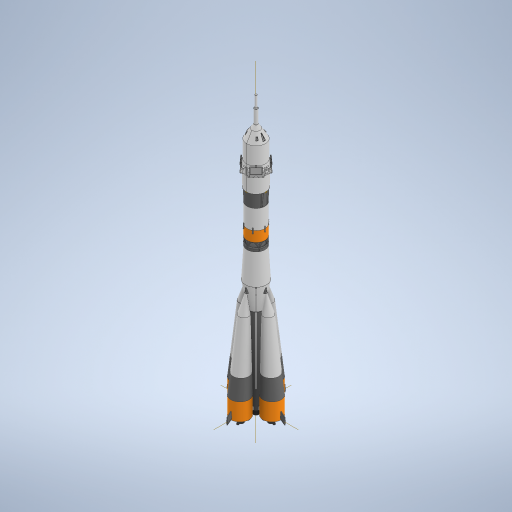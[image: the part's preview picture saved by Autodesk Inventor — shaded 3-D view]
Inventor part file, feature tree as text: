
AUTODESK INVENTOR PART (.ipt)
format: ipt  version: 2023 (Build 270158030, 158C)  size: 15,453,696 bytes
history: native  units: mm
features: fillet x71, sketch x70, extrude x63, other x23, plane x15, revolve x12, pattern_circular x11, sweep x6, mirror x3, chamfer x1, split x1
ambient origin geometry x8: Origin, YZ Plane, XZ Plane, XY Plane, X Axis, Y Axis, Z Axis, Center Point
bodies: Solid17 (feature_tree), Solid18 (feature_tree), Solid19 (feature_tree), Solid20 (feature_tree)
feature tree (276):
  other  "Soyuz Core Stage"
  extrude  "Core Airframe"  Depth=133.0mm TaperAngle=0.0deg
  extrude  "Vernier Housing"  Depth=3.4mm
  extrude  "Main Engine Extrude"  TaperAngle=0.0deg  [1 undecoded]
  extrude  "Main Engine Cut"  Depth=3.4mm
  extrude  "Vernier Nozzels"  Depth=3.4mm
  extrude  "Extrusion11"  Depth=3.4mm
  extrude  "Extrusion12"  Depth=5.5mm
  sweep  "Sweep1"
  sweep  "Booster Nosecone"
  extrude  "Extrusion16"  Depth=4.5mm
  plane  "Work Plane6"
  extrude  "Extrusion17"  Depth=4.5mm
  plane  "Work Plane5"
  extrude  "Extrusion18"  Depth=4.5mm
  fillet  "Fillet11"  Radius=4.5mm
  fillet  "Fillet12"  Radius=6.0mm
  fillet  "Fillet13"  Radius=2.0mm
  fillet  "Fillet14"  Radius=10.5mm
  extrude  "Booster Lock Extrusion"  Depth=2.0mm
  extrude  "Booster Lock Cut"  Depth=10.5mm
  other  "Work Point1"
  plane  "Work Plane1"
  sweep  "Sweep4"
  extrude  "Extrusion26"  TaperAngle=0.0deg  [1 undecoded]
  fillet  "Fillet16"  [1 undecoded]
  plane  "Work Plane4"
  other  "Work Point2"
  plane  "Work Plane2"
  extrude  "Extrusion27"  Depth=5.0mm
  extrude  "Extrusion28"  Depth=5.0mm
  extrude  "Extrusion29"  Depth=5.0mm
  fillet  "Fillet17"  [1 undecoded]
  fillet  "Fillet18"  [1 undecoded]
  fillet  "Fillet19"  [1 undecoded]
  extrude  "Extrusion30"  Depth=9.0mm
  fillet  "Fillet20"  Radius=28.0mm
  fillet  "Fillet21"  Radius=25.0mm
  fillet  "Fillet22"  [1 undecoded]
  extrude  "Extrusion31"  Depth=13.0mm
  extrude  "Extrusion32"  TaperAngle=0.0deg  [1 undecoded]
  extrude  "Extrusion33"  TaperAngle=0.0deg  [1 undecoded]
  extrude  "Extrusion34"  TaperAngle=0.0deg  [1 undecoded]
  fillet  "Fillet23"  [1 undecoded]
  fillet  "Fillet24"  Radius=17.0mm
  fillet  "Fillet25"  Radius=23.0mm
  fillet  "Fillet26"  [1 undecoded]
  extrude  "Extrusion35"  TaperAngle=0.0deg  [1 undecoded]
  extrude  "Extrusion36"  Depth=15.0mm
  extrude  "Extrusion50"  Depth=1.5mm
  fillet  "Fillet75"  [1 undecoded]
  extrude  "Extrusion51"  Depth=3.0mm TaperAngle=0.0deg
  extrude  "Extrusion52"  Depth=0.5mm TaperAngle=0.0deg
  other  "Work Point13"
  sketch  "Sketch86"  dims[d311=15.0mm d312=15.0mm]
  sweep  "Sweep6"
  revolve  "Revolution2"  [1 undecoded]
  pattern_circular  "Circular Pattern5"  [2 undecoded]
  mirror  "Mirror4"
  revolve  "Revolution3"  [1 undecoded]
  fillet  "Fillet76"  Radius=2.0mm
  fillet  "Fillet77"  Radius=21.5mm
  fillet  "Fillet78"  Radius=21.5mm
  fillet  "Fillet79"  Radius=6.2mm
  fillet  "Fillet80"  Radius=6.2mm
  fillet  "Fillet81"  Radius=0.5mm
  fillet  "Fillet82"  Radius=0.5mm
  fillet  "Fillet83"  Radius=0.5mm
  fillet  "Fillet84"  [1 undecoded]
  fillet  "Fillet85"  Radius=0.5mm
  fillet  "Fillet86"  Radius=1.3mm
  extrude  "Extrusion54"  TaperAngle=0.0deg  [1 undecoded]
  fillet  "Fillet91"  Radius=1.3mm
  fillet  "Fillet92"  Radius=3.0mm
  fillet  "Fillet93"  Radius=3.0mm
  pattern_circular  "Circular Pattern6"  [2 undecoded]
  plane  "Work Plane20"
  extrude  "Extrusion56"  TaperAngle=0.0deg  [1 undecoded]
  pattern_circular  "Circular Pattern8"  [2 undecoded]
  extrude  "Extrusion57"  Depth=1.0mm
  extrude  "Extrusion58"  Depth=0.5mm
  fillet  "Fillet94"  [1 undecoded]
  extrude  "Extrusion59"  TaperAngle=0.0deg  [1 undecoded]
  fillet  "Fillet95"  Radius=5.0mm
  pattern_circular  "Circular Pattern9"  [2 undecoded]
  extrude  "Extrusion60"  Depth=0.5mm
  fillet  "Fillet96"  [1 undecoded]
  extrude  "Extrusion61"  Depth=10.0mm TaperAngle=0.0deg
  fillet  "Fillet97"  Radius=0.5mm
  extrude  "Extrusion62"  Depth=0.5mm
  pattern_circular  "Circular Pattern11"  [2 undecoded]
  fillet  "Fillet98"  Radius=1.0mm
  extrude  "Extrusion63"  Depth=0.5mm
  fillet  "Fillet99"  Radius=0.5mm
  fillet  "Fillet100"  [1 undecoded]
  extrude  "Extrusion64"  TaperAngle=0.0deg  [1 undecoded]
  extrude  "Extrusion65"  TaperAngle=0.0deg  [1 undecoded]
  extrude  "Extrusion66"  TaperAngle=0.0deg  [1 undecoded]
  extrude  "Extrusion67"  Depth=0.5mm TaperAngle=0.0deg
  fillet  "Fillet101"  Radius=3.0mm
  plane  "Work Plane24"
  extrude  "Extrusion68"  Depth=0.5mm
  fillet  "Fillet102"  Radius=0.1mm
  extrude  "Extrusion69"  Depth=0.5mm
  pattern_circular  "Circular Pattern12"  [2 undecoded]
  extrude  "Extrusion70"  TaperAngle=0.0deg  [1 undecoded]
  fillet  "Fillet103"  [1 undecoded]
  pattern_circular  "Circular Pattern13"  [2 undecoded]
  extrude  "Extrusion71"  TaperAngle=0.0deg  [1 undecoded]
  extrude  "Extrusion72"  TaperAngle=0.0deg  [1 undecoded]
  extrude  "Extrusion73"  TaperAngle=0.0deg  [1 undecoded]
  fillet  "Fillet105"  [1 undecoded]
  extrude  "Extrusion74"  TaperAngle=0.0deg  [1 undecoded]
  extrude  "Extrusion75"  TaperAngle=0.0deg  [1 undecoded]
  fillet  "Fillet106"  [1 undecoded]
  fillet  "Fillet107"  [1 undecoded]
  other  "Work Point16"
  revolve  "Revolution6"  [1 undecoded]
  other  "Work Point17"
  plane  "Work Plane26"
  extrude  "Extrusion81"  Depth=0.5mm
  fillet  "Fillet114"  Radius=12.5mm
  fillet  "Fillet115"  Radius=12.5mm
  fillet  "Fillet116"  Radius=12.5mm
  fillet  "Fillet117"  [1 undecoded]
  mirror  "Mirror6"
  sweep  "Sweep8"
  pattern_circular  "Circular Pattern14"  [2 undecoded]
  extrude  "Extrusion80"  TaperAngle=0.0deg  [1 undecoded]
  revolve  "Revolution5"  [1 undecoded]
  extrude  "Extrusion82"  TaperAngle=0.0deg  [1 undecoded]
  fillet  "Fillet118"  [1 undecoded]
  other  "Work Point18"
  plane  "Work Plane27"
  extrude  "Extrusion83"  TaperAngle=0.0deg  [1 undecoded]
  sweep  "Sweep9"
  revolve  "Revolution7"  [1 undecoded]
  revolve  "Revolution8"  [1 undecoded]
  revolve  "Revolution9"  [1 undecoded]
  revolve  "Revolution10"  [1 undecoded]
  fillet  "Fillet119"  Radius=6.0mm
  fillet  "Fillet120"  Radius=6.0mm
  fillet  "Fillet121"  Radius=6.0mm
  fillet  "Fillet122"  [1 undecoded]
  fillet  "Fillet123"  [1 undecoded]
  fillet  "Fillet124"  Radius=5.0mm
  plane  "Work Plane30"
  extrude  "Extrusion85"  Depth=1.0mm
  extrude  "Extrusion86"  Depth=1.0mm
  extrude  "Extrusion87"  Depth=0.5mm
  extrude  "Extrusion88"  Depth=0.5mm
  fillet  "Fillet125"  Radius=1.0mm
  fillet  "Fillet126"  [1 undecoded]
  fillet  "Fillet127"  Radius=2.0mm
  fillet  "Fillet128"  [1 undecoded]
  extrude  "Extrusion89"  Depth=0.5mm
  extrude  "Extrusion90"  Depth=1.0mm
  fillet  "Fillet129"  [1 undecoded]
  fillet  "Fillet130"  Radius=1.0mm
  fillet  "Fillet131"  Radius=0.781667mm
  extrude  "Extrusion92"  Depth=0.5mm
  extrude  "Extrusion93"  Depth=0.5mm
  fillet  "Fillet134"  Radius=12.5mm
  fillet  "Fillet135"  Radius=0.5mm
  fillet  "Fillet136"  [1 undecoded]
  fillet  "Fillet138"  Radius=0.5mm
  pattern_circular  "Circular Pattern15"  [2 undecoded]
  other  "Work Point19"
  plane  "Work Plane31"
  extrude  "Extrusion94"  Depth=0.5mm
  fillet  "Fillet139"  [1 undecoded]
  revolve  "Revolution11"  [1 undecoded]
  chamfer  "Chamfer3"  Distance=1.377412mm
  fillet  "Fillet140"  Radius=1.377mm
  fillet  "Fillet141"  Radius=4.5mm
  fillet  "Fillet142"  Radius=1.0mm
  plane  "Work Plane32"
  revolve  "Revolution12"  [1 undecoded]
  fillet  "Fillet143"  Radius=4.5mm
  pattern_circular  "Circular Pattern16"  [2 undecoded]
  fillet  "Fillet144"  Radius=1.0mm
  pattern_circular  "Circular Pattern17"  [2 undecoded]
  mirror  "Mirror7"
  split  "Split1"
  sketch  "Sketch5"  dims[d0=20.0mm d1=133.0mm d2=0.0mm]
  sketch  "Sketch6"  dims[d7=0.0mm d9=3.4mm]
  sketch  "Sketch15"  dims[d10=3.4mm d12=0.0mm]
  sketch  "Sketch16"  dims[d15=3.4mm d18=3.4mm]
  other  "Soyuz Booster"
  sketch  "Sketch28"  dims[d20=3.4mm d21=3.4mm]
  sketch  "Sketch29"  dims[d25=3.4mm d26=3.4mm]
  sketch  "Sketch31"  dims[d33=7.0mm d34=0.0mm d47=5.5mm]
  sketch  "Sketch34"  dims[d48=5.5mm d49=5.5mm]
  sketch  "Sketch35"  dims[d50=5.5mm d52=4.5mm]
  sketch  "Sketch42"  dims[d57=4.5mm d58=4.5mm d59=4.5mm d60=6.0mm d61=2.094395mm d62=2.0mm d63=10.5mm]
  sketch  "Sketch43"  dims[d64=2.0mm d65=2.0mm]
  sketch  "Sketch45"  dims[d66=2.0mm d67=10.5mm]
  sketch  "Sketch51"  dims[d68=10.5mm d69=10.5mm]
  sketch  "Sketch52"  dims[d70=0.0mm d71=0.0mm d72=0.0mm]
  sketch  "Sketch53"  dims[d73=0.0mm d74=5.0mm d75=1.396263mm]
  sketch  "Sketch54"  dims[d76=5.0mm d77=5.0mm]
  sketch  "Sketch55"  dims[d78=5.0mm d79=5.0mm d80=0.0mm d81=0.0mm d82=0.0mm]
  sketch  "Sketch56"  dims[d83=0.0mm d85=9.0mm d86=-1.396263mm d156=28.0mm d160=25.0mm d161=0.0mm]
  other  "Core Stage Part 2"
  sketch  "Sketch57"  dims[d166=13.0mm d167=13.0mm d168=13.0mm d171=13.0mm]
  sketch  "Sketch81"  dims[d174=27.0mm d175=0.0mm d177=0.0mm]
  sketch  "Sketch82"  dims[d178=0.0mm d179=0.0mm]
  sketch  "Sketch83"  dims[d180=38.0mm d181=1.658063mm d236=0.0mm d237=0.0mm d278=17.0mm d280=23.0mm d281=-0.610865mm d282=0.0mm]
  other  "Interstage 1"
  sketch  "Sketch85"  dims[d304=0.0mm d309=0.0mm]
  other  "Srf3"
  sketch  "3D Sketch5"
  other  "Project to Surface5"
  sketch  "Sketch87"  dims[d313=19.0mm d314=1.5mm d316=-2.356194mm d317=0.0mm]
  other  "Project to Surface7"
  sketch  "Sketch88"  dims[d318=0.0mm d330=3.0mm d331=0.0mm]
  sketch  "Sketch89"  dims[d334=0.5mm d335=0.0mm d338=0.5mm d339=0.0mm]
  sketch  "Sketch91"  dims[d342=3.0mm d343=3.0mm]
  plane  "Work Plane19"
  sketch  "Sketch93"  dims[d344=3.0mm d345=6.0mm]
  sketch  "Sketch94"  dims[d346=1.2mm]
  other  "Interstage 2"
  sketch  "Sketch95"  dims[d347=1.2mm]
  other  "2nd Stage"
  sketch  "Sketch96"  dims[d348=1.2mm]
  sketch  "Sketch97"  dims[d349=1.2mm]
  sketch  "Sketch100"  dims[d350=0.0mm]
  other  "Srf4"
  sketch  "Sketch103"  dims[d351=0.0mm]
  sketch  "Sketch104"  dims[d352=0.0mm]
  sketch  "Sketch105"  dims[d353=0.0mm]
  sketch  "Sketch107"  dims[d354=14.5mm]
  sketch  "Sketch108"  dims[d355=14.5mm]
  sketch  "Sketch109"  dims[d356=14.5mm]
  sketch  "Sketch111"  dims[d357=14.5mm]
  sketch  "Sketch112"  dims[d358=11.5mm d359=1.745329mm]
  sketch  "Sketch113"  dims[d361=2.2mm]
  sketch  "Sketch114"  dims[d362=1.6mm]
  sketch  "Sketch115"  dims[d363=0.0mm]
  sketch  "Sketch116"  dims[d364=4.1mm d365=-1.745329mm]
  other  "2nd Stage Part 2"
  sketch  "Sketch117"  dims[d366=0.0mm]
  sketch  "Sketch118"  dims[d367=1.6mm]
  sketch  "Sketch120"  dims[d368=2.2mm]
  sketch  "Sketch121"  dims[d369=0.0mm]
  sketch  "Sketch128"  dims[d370=1.6mm]
  other  "Fairing"
  sketch  "Sketch130"  dims[d371=2.2mm]
  sketch  "Sketch132"  dims[d372=1.6mm]
  sketch  "Sketch134"  dims[d373=0.0mm]
  sketch  "Sketch135"  dims[d374=2.2mm]
  sketch  "Sketch139"  dims[d397=5.5mm d398=4.5mm d400=5.5mm d401=4.5mm d402=4.5mm d403=5.5mm d404=4.5mm d406=5.5mm d410=2.094395mm d411=6.0mm]
  sketch  "Sketch140"  dims[d412=5.0mm d413=0.0mm d414=5.0mm d415=0.0mm d416=0.0mm d417=5.0mm d418=0.0mm d419=5.0mm d421=-1.396263mm d422=9.0mm]
  other  "Escape Tower"
  plane  "Work Plane28"
  plane  "Work Plane29"
  other  "Grid Fins"
  sketch  "Sketch145"  dims[d423=0.0mm]
  sketch  "Sketch146"  dims[d424=0.0mm]
  sketch  "Sketch149"  dims[d425=0.0mm]
  sketch  "Sketch150"  dims[d426=0.0mm]
  sketch  "Sketch152"  dims[d427=9.0mm]
  sketch  "Sketch153"  dims[d428=9.0mm]
  sketch  "Sketch154"  dims[d429=9.0mm]
  sketch  "Sketch156"  dims[d430=9.0mm]
  sketch  "Sketch157"  dims[d431=6.0mm]
  other  "Pattern of Fairing:1"
  other  "Pattern of Grid Fins:2"
  sketch  "Sketch159"  dims[d432=0.0mm d446=1.396263mm d447=5.0mm d449=2.0mm d450=2.0mm d452=21.5mm d453=21.5mm d454=6.2mm d455=6.2mm d456=0.5mm d459=0.5mm d460=0.5mm d461=0.0mm d464=0.5mm d465=1.3mm d466=0.0mm d467=1.3mm d468=3.0mm d470=3.0mm d472=0.0mm d473=0.0mm d475=6.0mm d476=1.0mm d477=6.0mm d478=0.0mm d479=-0.202458mm d480=0.0mm d481=5.0mm d482=2.0mm d483=2.0mm d484=0.0mm d485=10.0mm d486=0.0mm d487=0.5mm d489=3.0mm d490=1.0mm d491=1.0mm d492=28.0mm d493=0.5mm d494=0.0mm d518=0.0mm d521=0.0mm d522=0.0mm d524=0.0mm d525=0.5mm d526=0.0mm d527=3.0mm d528=3.0mm d529=0.1mm d530=20.0mm d531=7.0mm d532=0.0mm d538=0.0mm d539=0.0mm d540=0.0mm d541=0.0mm d542=0.0mm d543=0.0mm d544=0.0mm d545=0.0mm d546=0.0mm d547=0.0mm d548=0.0mm d549=0.0mm d550=12.5mm d551=12.5mm d553=12.5mm d554=12.5mm d556=0.0mm d557=0.0mm d561=0.0mm d562=0.0mm d563=0.0mm d564=0.0mm d566=0.0mm d567=0.0mm d568=0.0mm d571=0.0mm d572=0.0mm d573=0.0mm d575=6.0mm d576=6.0mm d577=6.0mm d578=6.0mm d579=0.0mm d581=0.0mm d582=5.0mm d583=-6.108652mm d584=1.0mm d585=1.0mm d593=2.0mm d594=3.0mm d604=1.0mm d608=0.0mm d609=2.0mm d610=0.0mm d611=3.0mm d612=1.0mm d614=0.0mm d617=1.0mm d618=0.781667mm d619=2.5mm d649=12.5mm d650=12.5mm d651=0.5mm d652=0.0mm d653=0.5mm d654=4.5mm d655=4.5mm d657=0.0mm d658=1.0mm d659=1.377412mm d660=1.377mm d661=4.5mm d662=1.0mm d663=0.5mm d664=0.0mm d665=4.5mm d666=1.377mm d667=1.0mm d668=4.5mm d669=1.377mm d670=1.0mm d671=0.5mm d672=0.0mm d673=4.5mm d674=1.377mm d675=4.5mm d676=1.377mm d677=1.0mm d678=1.0mm d679=0.5mm d680=0.0mm d681=4.5mm d682=4.5mm d683=1.377mm d684=1.377mm d685=1.0mm d686=1.0mm d687=0.5mm d688=0.0mm d689=0.5mm d690=0.2mm d691=0.3mm d692=1.0mm d694=0.0mm d695=0.0mm d696=0.1mm d697=5.0mm d698=0.0mm d699=0.0mm d700=0.0mm d702=50.0mm d703=-0.541052mm d709=0.0mm d993=0.0mm d994=0.0mm d995=2.5mm d996=5.0mm d997=0.0mm d998=8.0mm d999=0.0mm d1000=0.0mm d1001=0.0mm d1002=0.0mm d1003=0.0mm d1004=0.0mm d1005=4.0mm d1006=0.0mm d1007=0.0mm d1008=0.0mm d1009=0.0mm d1010=0.0mm d1011=0.0mm d1012=0.0mm d1013=4.1mm d1014=0.0mm d1026=45.0deg d1030=0.0mm d1031=0.0mm d1034=10.0mm d1035=3.0mm d1036=0.0mm d1037=0.0mm d1038=0.1mm d1039=0.0mm d1040=2.5mm d1041=2.5mm d1042=0.9mm d1048=2.5mm d1049=2.6mm d1050=90.0deg d1051=60.0mm d1052=360.0deg d1054=1.5mm d1057=0.4mm d1058=90.0deg d1059=0.2mm d1060=0.7mm d1061=0.4mm d1062=1.0mm d1063=0.5mm d1064=0.2mm d1065=0.2mm d1066=0.2mm d1067=0.2mm d1068=0.2mm d1069=0.2mm d1070=0.1mm d1083=0.5mm d1084=0.3mm d1085=2.0mm d1086=0.0mm d1087=1.3mm d1088=0.0mm d1089=0.7mm d1090=0.5mm d1091=0.7mm d1092=60.0mm d1093=360.0deg d1103=-1.0mm d1104=0.0mm d1105=0.0mm d1106=0.0mm d1107=0.0mm d1108=30.0mm d1109=1.25mm d1110=1.4mm d1111=0.0mm d1112=1.25mm d1116=40.0mm d1117=360.0deg d1119=0.0mm d1120=0.0mm d1121=0.0mm d1122=0.0mm d1123=0.0mm d1124=0.0mm d1125=16.0mm d1126=0.0mm d1127=0.0mm d1128=0.0mm d1129=0.0mm d1130=30.0mm d1131=0.0mm d1132=0.1mm d1133=1.7mm d1134=14.0mm d1135=5.0mm d1136=0.0mm d1137=0.8mm d1138=60.0mm d1139=360.0deg d1141=0.0mm d1142=3.0mm d1143=0.0mm d1144=0.5mm d1145=1.0mm d1146=6.0mm d1147=0.0mm d1148=8.0mm d1149=0.0mm d1150=3.0mm d1151=9.0mm d1152=6.981317mm d1153=9.6mm d1154=90.0deg d1193=3.5mm d1194=1.2mm d1195=0.0mm d1196=2.5mm d1197=1.8mm d1200=2.0mm d1201=10.0mm d1203=0.3mm d1204=0.2mm d1205=9.397169mm d1206=1.165699mm d1207=1.2mm d1208=2.0mm d1209=2.0mm d1210=0.0mm d1211=60.0mm d1212=360.0deg d1214=8.0mm d1215=0.0mm d1216=0.0mm d1217=20.0mm d1218=2.0mm d1219=0.0mm d1220=0.2mm d1221=0.2mm d1222=5.5mm d1223=4.5mm d1224=4.5mm d1228=5.0mm d1229=4.0mm d1230=2.094395mm d1231=-2.094395mm d1232=0.0mm d1233=0.0mm d1234=0.0mm d1235=5.0mm d1236=4.014257mm d1238=0.0mm d1239=0.0mm d1240=1.5mm d1241=10.5mm d1242=-1.396263mm d1243=2.0mm d1244=8.5mm d1245=0.0mm d1246=4.0mm d1247=1.745329mm d1248=0.8mm d1249=1.5mm d1250=3.0mm d1251=8.5mm d1252=2.8mm d1253=0.0mm d1254=1.4mm d1258=6.8mm d1259=0.872665mm d1260=0.0mm d1261=0.0mm d1262=0.0mm d1263=0.0mm d1264=0.55mm d1265=0.0mm d1266=40.0mm d1267=360.0deg d1270=0.0mm d1271=0.0mm d1272=0.0mm d1273=3.55mm d1274=0.0mm d1275=0.8mm d1276=60.0mm d1277=360.0deg d1282=20.0mm d1283=0.349066mm d1286=4.0mm d1287=0.0mm d1288=0.2mm d1289=1.0mm d1290=0.0mm d1291=0.2mm d1292=3.5mm d1293=5.0mm d1294=7.0mm d1295=0.0mm d1296=5.0mm d1297=5.0mm d1298=0.0mm d1299=1.0mm d1300=1.0mm d1310=0.0mm d1311=0.0mm d1313=11.5mm d1316=0.3mm d1317=0.3mm d1318=3.066164mm d1319=2.367748mm d1320=9.41mm d1321=4.705mm d1324=1.81mm d1330=0.0mm d1331=0.0mm d1333=3.0mm d1361=20.0mm d1362=360.0deg d1372=0.0mm d1375=0.0mm d1391=1.0mm d1392=1.3mm d1393=2.0mm d1394=2.0mm d1395=2.0mm d1396=2.0mm d1397=1.0mm d1398=1.0mm d1399=1.0mm d1400=1.0mm d1401=1.0mm d1402=1.0mm d1403=13.566164mm d1404=12.266164mm d1405=13.566164mm d1406=12.266164mm d1407=13.566164mm d1408=12.266164mm d1409=13.566164mm d1410=12.266164mm d1411=2.0mm d1412=90.0deg d1413=1.2mm d1414=2.5mm d1417=3.0mm d1418=0.0mm d1424=3.0mm d1425=15.53343mm d1429=180.0deg d1430=23.0mm d1431=12.2mm d1432=45.0deg d1433=2.5mm d1434=2.5mm d1435=3.4mm d1436=3.4mm d1437=0.0mm d1438=0.0mm d1439=1.3mm d1440=0.0mm d1441=0.5mm d1442=0.4mm d1443=0.4mm d1444=0.4mm d1445=11.586164mm d1446=0.0mm d1447=0.0mm d1448=0.0mm d1449=0.0mm d1452=0.0mm d1453=1.3mm d1454=0.0mm d1455=0.0mm d1456=0.0mm d1458=13.566164mm d1459=12.266164mm d1460=12.266164mm d1461=13.566164mm d1462=2.0mm d1463=1.5mm d1464=0.0mm d1465=0.1mm d1469=5.0mm d1470=5.0mm d1471=20.0mm d1473=1.071mm d1474=0.0mm d1475=0.0mm d1476=0.0mm d1477=0.0mm d1478=0.0mm d1479=0.0mm d1482=19.3mm d1483=0.0mm d1484=16.057029mm d1485=3.0mm d1486=0.0mm d1487=0.0mm d1490=0.0mm d1497=15.184364mm d1498=15.0mm d1499=180.0deg d1500=27.0mm d1501=15.620697mm d1502=180.0deg d1504=60.0deg d1513=13.856406mm d1514=180.0deg d1528=14.0mm d1529=3.579724mm d1531=1.0mm d1532=1.000457mm d1533=0.917096mm d1534=1.0mm d1540=2.0mm d1541=1.329428mm d1543=1.5mm d1545=4.997278mm d1546=0.0mm d1547=3.0mm d1552=2.7mm d1554=30.892328mm d1555=2.0mm d1556=3.250296mm d1557=6.497278mm d1560=0.0mm d1561=21.46755mm d1562=25.0mm d1563=1.5mm d1564=0.0mm d1566=20.071286mm d1567=37.0mm d1568=1.0mm d1569=1.0mm d1570=27.0mm d1571=45.0mm d1572=90.0deg d1574=0.917096mm d1575=0.4mm d1576=0.4mm d1577=0.4mm d1578=0.1mm d1579=0.1mm d1580=0.2mm d1583=2.0mm d1593=1.0mm d1594=1.0mm d1596=0.5mm d1597=2.5mm d1598=3.5mm d1599=3.5mm d1600=3.5mm d1601=2.0mm d1602=0.0mm d1603=0.7mm d1604=0.7mm d1605=4.0mm d1606=0.7mm d1607=0.7mm d1608=0.0mm d1609=0.0mm d1610=0.0mm d1611=0.0mm d1612=0.0mm d1613=0.3mm d1614=0.0mm d1615=0.2mm d1616=2.0mm d1617=1.0mm d1618=2.0mm d1619=1.0mm d1621=100.0mm d1622=2.0mm d1623=2.0mm d1624=2.0mm d1625=0.0mm d1626=0.0mm d1627=0.9mm d1628=0.1mm d1629=0.1mm d1630=0.1mm d1632=1.0mm d1633=0.75mm d1634=0.75mm d1635=0.0mm d1636=0.0mm d1640=7.0mm d1641=7.0mm d1642=3.5mm d1643=0.7mm d1644=6.0mm d1645=0.0mm d1646=2.0mm d1649=0.0mm d1650=2.0mm d1651=2.25mm d1652=4.5mm d1653=0.0mm d1654=0.0mm d1655=4.0mm d1656=1.0mm d1657=0.5mm d1667=1.0mm d1668=0.0mm d1669=0.0mm d1670=0.0mm d1674=0.8mm d1676=0.8mm d1677=0.5mm d1678=0.5mm d1679=1.5mm d1680=1.7mm d1681=0.0mm d1682=2.0mm d1683=0.2mm d1684=0.1mm d1686=0.1mm d1687=20.0mm d1688=90.0deg d1690=3.5mm d1691=0.0mm d1692=4.5mm d1693=4.5mm d1694=0.0mm d1695=2.0mm d1696=0.0mm d1697=1.0mm d1698=4.0mm d1699=2.0mm d1700=45.0deg d1701=12.0mm d1702=3.0mm d1703=10.7mm d1705=5.0mm d1706=12.0mm d1707=2.443461mm d1708=1.0mm d1709=2.0mm d1710=45.0deg d1711=0.5mm d1712=0.5mm d1713=0.5mm d1714=4.5mm d1715=5.5mm d1716=8.0mm d1717=8.5mm d1718=9.424778mm d1719=3.3mm d1720=2.3mm d1721=1.745329mm d1722=0.5mm d1723=20.0mm d1724=19.198622mm d1726=0.5mm d1731=0.5mm d1732=0.5mm d1733=0.5mm d1734=0.5mm d1735=0.5mm d1736=0.5mm d1737=0.5mm d1738=0.5mm d1739=0.5mm d1740=0.5mm d1741=0.5mm d1742=0.5mm d1743=0.5mm d1744=0.5mm d1745=0.5mm d1746=0.5mm d1747=0.5mm d1748=0.5mm d1749=0.5mm d1755=0.5mm d1756=0.5mm d1757=0.5mm d1758=0.5mm d1759=0.5mm d1760=0.5mm d1763=0.5mm d1764=0.5mm d1766=0.5mm d1767=0.5mm d1768=0.5mm d1769=0.5mm d1770=0.5mm d1771=0.5mm d1772=0.5mm d1773=0.5mm d1774=0.5mm d1775=0.5mm d1776=0.5mm d1777=0.5mm d1778=0.5mm d1779=0.5mm d1780=0.5mm d1781=0.5mm d1782=0.5mm d1783=0.5mm d1784=0.5mm d1785=0.5mm d1786=0.5mm d1787=0.5mm d1788=0.5mm d1789=0.5mm d1790=0.5mm d1791=0.5mm d1792=0.5mm d1793=0.5mm d1794=20.0mm d1795=90.0deg d194=0.5mm d195=0.872665mm d196=0.5mm d197=0.872665mm d261=0.5mm d262=0.872665mm d263=0.5mm d264=0.872665mm d808=0.5mm d809=0.872665mm d810=0.5mm d811=0.872665mm d1255=0.872665mm d1351=0.5mm d1352=0.872665mm d1353=0.5mm d1354=0.872665mm]
  extrude  "Extrusion23"  Depth=0.5mm
  extrude  "Extrusion24"  Depth=1.0mm
  extrude  "Extrusion25"  Depth=0.5mm TaperAngle=0.0deg
  revolve  "RevolutionSrf2"  [1 undecoded]
  revolve  "RevolutionSrf3"  [1 undecoded]
  sketch  "Sketch39"  dims[d53=4.5mm d54=4.5mm]
  sketch  "Sketch40"  dims[d55=4.5mm d56=4.5mm]
note: 80 required parameter values undecoded (feature->parameter linkage not recoverable at this tier; creation-order binding heuristic only, values carry confidence <= 0.55)